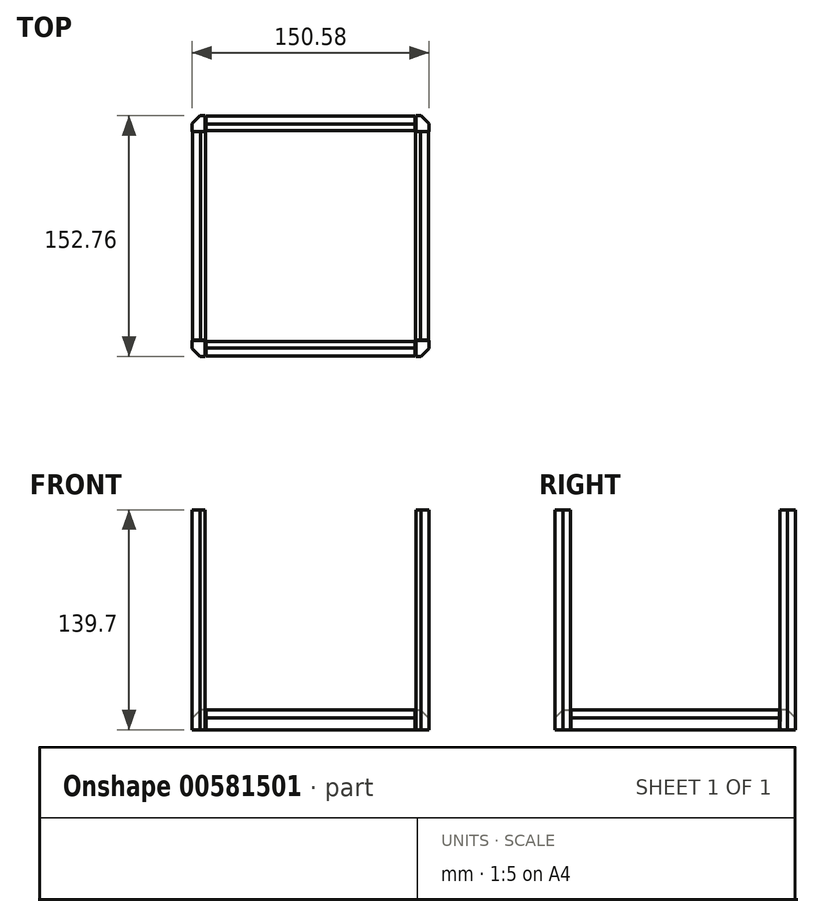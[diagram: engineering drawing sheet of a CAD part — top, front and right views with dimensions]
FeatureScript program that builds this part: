
annotation { "Feature Type Name" : "Feature", "Feature Type Description" : "" }
export const myFeature = defineFeature(function(context is Context, id is Id, definition is map)
    precondition{}
    {
        {
            var Q0;
            Q0=qCreatedBy(makeId("Top.planeOp"),FACE);
            var sketch = newSketch(context, id + "F0", { "sketchPlane" : qUnion([Q0])});
            skLineSegment(sketch, "E0.bottom", {"start": v(-75.29, 76.38) * mm, "end": v(-66.89, 76.38) * mm});
            skLineSegment(sketch, "E0.top", {"start": v(-75.29, 66.46) * mm, "end": v(-66.89, 66.46) * mm});
            skLineSegment(sketch, "E0.left", {"start": v(-75.29, 76.38) * mm, "end": v(-75.29, 66.46) * mm});
            skLineSegment(sketch, "E0.right", {"start": v(-66.89, 76.38) * mm, "end": v(-66.89, 66.46) * mm});
            skSolve(sketch);
        }
        {
            var Q0;
            Q0 = qSketchRegion(id + "F0", true);
            extrude(context, id + "F1", {"entities" : qUnion([Q0]), "depth" : 139.7 * mm, "offsetDistance" : 25.4 * mm});
        }
        {
            var Q0;
            Q0=makeQuery(id+"F1.opExtrude","SWEPT_BODY",BODY,{"disambiguationData":[OSD([sQuery(id+"F0.wireOp",EDGE,"E0.bottom"),sQuery(id+"F0.wireOp",EDGE,"E0.top"),sQuery(id+"F0.wireOp",EDGE,"E0.left"),sQuery(id+"F0.wireOp",EDGE,"E0.right")])]});
            var Q1;
            Q1=qCreatedBy(makeId("Right.planeOp"),FACE);
            mirror(context, id + "F2", {"entities" : qUnion([Q0]), "mirrorPlane" : qUnion([Q1])});
        }
        {
            var Q0;
            Q0=makeQuery(id+"F2.opPattern","COPY",BODY,{"derivedFrom":makeQuery(id+"F1.opExtrude","SWEPT_BODY",BODY,{"disambiguationData":[OSD([sQuery(id+"F0.wireOp",EDGE,"E0.bottom"),sQuery(id+"F0.wireOp",EDGE,"E0.top"),sQuery(id+"F0.wireOp",EDGE,"E0.left"),sQuery(id+"F0.wireOp",EDGE,"E0.right")])]}),"instanceName":"1"});
            var Q1;
            Q1=qCreatedBy(makeId("Front.planeOp"),FACE);
            mirror(context, id + "F3", {"entities" : qUnion([Q0]), "mirrorPlane" : qUnion([Q1])});
        }
        {
            var Q0;
            Q0=makeQuery(id+"F3.opPattern","COPY",BODY,{"derivedFrom":makeQuery(id+"F2.opPattern","COPY",BODY,{"derivedFrom":makeQuery(id+"F1.opExtrude","SWEPT_BODY",BODY,{"disambiguationData":[OSD([sQuery(id+"F0.wireOp",EDGE,"E0.bottom"),sQuery(id+"F0.wireOp",EDGE,"E0.top"),sQuery(id+"F0.wireOp",EDGE,"E0.left"),sQuery(id+"F0.wireOp",EDGE,"E0.right")])]}),"instanceName":"1"}),"instanceName":"1"});
            var Q1;
            Q1=qCreatedBy(makeId("Right.planeOp"),FACE);
            mirror(context, id + "F4", {"entities" : qUnion([Q0]), "mirrorPlane" : qUnion([Q1])});
        }
        {
            var Q0;
            Q0=qCreatedBy(makeId("Top.planeOp"),FACE);
            var sketch = newSketch(context, id + "F5", { "sketchPlane" : qUnion([Q0])});
            skLineSegment(sketch, "E1.bottom", {"start": v(-66.65, 66.31) * mm, "end": v(-75.03, 66.31) * mm});
            skLineSegment(sketch, "E1.top", {"start": v(-66.65, -66.13) * mm, "end": v(-75.03, -66.13) * mm});
            skLineSegment(sketch, "E1.left", {"start": v(-66.65, 66.31) * mm, "end": v(-66.65, -66.13) * mm});
            skLineSegment(sketch, "E1.right", {"start": v(-75.03, 66.31) * mm, "end": v(-75.03, -66.13) * mm});
            skSolve(sketch);
        }
        {
            var Q0;
            Q0 = qSketchRegion(id + "F5", true);
            extrude(context, id + "F6", {"entities" : qUnion([Q0]), "depth" : 12.7 * mm, "offsetDistance" : 25.4 * mm});
        }
        {
            var Q0;
            Q0=makeQuery(id+"F6.opExtrude","SWEPT_BODY",BODY,{"disambiguationData":[OSD([sQuery(id+"F5.wireOp",EDGE,"E1.bottom"),sQuery(id+"F5.wireOp",EDGE,"E1.top"),sQuery(id+"F5.wireOp",EDGE,"E1.left"),sQuery(id+"F5.wireOp",EDGE,"E1.right")])]});
            var Q1;
            Q1=makeQuery(id+"F1.opExtrude","SWEPT_BODY",BODY,{"disambiguationData":[OSD([sQuery(id+"F0.wireOp",EDGE,"E0.bottom"),sQuery(id+"F0.wireOp",EDGE,"E0.top"),sQuery(id+"F0.wireOp",EDGE,"E0.left"),sQuery(id+"F0.wireOp",EDGE,"E0.right")])]});
            var Q2;
            Q2=qCreatedBy(makeId("Right.planeOp"),FACE);
            mirror(context, id + "F7", {"operationType" : NewBodyOperationType.ADD, "entities" : qUnion([Q0, Q1]), "mirrorPlane" : qUnion([Q2])});
        }
        {
            var Q0;
            Q0=qCreatedBy(makeId("Top.planeOp"),FACE);
            var sketch = newSketch(context, id + "F8", { "sketchPlane" : qUnion([Q0])});
            skLineSegment(sketch, "E2.bottom", {"start": v(-66.46, -76.25) * mm, "end": v(66.33, -76.25) * mm});
            skLineSegment(sketch, "E2.top", {"start": v(-66.46, -67.1) * mm, "end": v(66.33, -67.1) * mm});
            skLineSegment(sketch, "E2.left", {"start": v(-66.46, -76.25) * mm, "end": v(-66.46, -67.1) * mm});
            skLineSegment(sketch, "E2.right", {"start": v(66.33, -76.25) * mm, "end": v(66.33, -67.1) * mm});
            skSolve(sketch);
        }
        {
            var Q0;
            Q0 = qSketchRegion(id + "F8", true);
            extrude(context, id + "F9", {"entities" : qUnion([Q0]), "depth" : 12.7 * mm, "offsetDistance" : 25.4 * mm});
        }
        {
            var Q0;
            Q0=makeQuery(id+"F9.opExtrude","SWEPT_BODY",BODY,{"disambiguationData":[OSD([sQuery(id+"F8.wireOp",EDGE,"E2.bottom"),sQuery(id+"F8.wireOp",EDGE,"E2.top"),sQuery(id+"F8.wireOp",EDGE,"E2.left"),sQuery(id+"F8.wireOp",EDGE,"E2.right")])]});
            var Q1;
            Q1=qCreatedBy(makeId("Front.planeOp"),FACE);
            mirror(context, id + "F10", {"entities" : qUnion([Q0]), "mirrorPlane" : qUnion([Q1])});
        }
        {
            var Q0;
            Q0=makeQuery(id+"F3.opPattern","COPY",EDGE,{"derivedFrom":makeQuery(id+"F2.opPattern","COPY",EDGE,{"derivedFrom":makeQuery(id+"F1.opExtrude","SWEPT_EDGE",EDGE,{"disambiguationData":[OSD([sQuery(id+"F0.wireOp",EDGE,"E0.bottom"),sQuery(id+"F0.wireOp",EDGE,"E0.left")])]}),"instanceName":"1"}),"instanceName":"1"});
            var Q1;
            Q1=makeQuery(id+"F2.opPattern","COPY",EDGE,{"derivedFrom":makeQuery(id+"F1.opExtrude","SWEPT_EDGE",EDGE,{"disambiguationData":[OSD([sQuery(id+"F0.wireOp",EDGE,"E0.bottom"),sQuery(id+"F0.wireOp",EDGE,"E0.left")])]}),"instanceName":"1"});
            var Q2;
            Q2=makeQuery(id+"F4.opPattern","COPY",EDGE,{"derivedFrom":makeQuery(id+"F3.opPattern","COPY",EDGE,{"derivedFrom":makeQuery(id+"F2.opPattern","COPY",EDGE,{"derivedFrom":makeQuery(id+"F1.opExtrude","SWEPT_EDGE",EDGE,{"disambiguationData":[OSD([sQuery(id+"F0.wireOp",EDGE,"E0.bottom"),sQuery(id+"F0.wireOp",EDGE,"E0.left")])]}),"instanceName":"1"}),"instanceName":"1"}),"instanceName":"1"});
            var Q3;
            Q3=makeQuery(id+"F1.opExtrude","SWEPT_EDGE",EDGE,{"disambiguationData":[OSD([sQuery(id+"F0.wireOp",EDGE,"E0.bottom"),sQuery(id+"F0.wireOp",EDGE,"E0.left")])]});
            chamfer(context, id + "F11", {"entities" : qUnion([Q0, Q1, Q2, Q3]), "width" : 5.08 * mm, "tangentPropagation" : true});
        }
        {
            var Q0;
            Q0=makeQuery(id+"F9.opExtrude","CAP_EDGE",EDGE,{"disambiguationData":[OSD([sQuery(id+"F8.wireOp",EDGE,"E2.bottom")])],"isStart":false});
            var Q1;
            Q1=makeQuery(id+"F7.opPattern","COPY",EDGE,{"derivedFrom":makeQuery(id+"F6.opExtrude","CAP_EDGE",EDGE,{"disambiguationData":[OSD([sQuery(id+"F5.wireOp",EDGE,"E1.right")])],"isStart":false}),"instanceName":"1"});
            var Q2;
            Q2=makeQuery(id+"F10.opPattern","COPY",EDGE,{"derivedFrom":makeQuery(id+"F9.opExtrude","CAP_EDGE",EDGE,{"disambiguationData":[OSD([sQuery(id+"F8.wireOp",EDGE,"E2.bottom")])],"isStart":false}),"instanceName":"1"});
            var Q3;
            Q3=makeQuery(id+"F6.opExtrude","CAP_EDGE",EDGE,{"disambiguationData":[OSD([sQuery(id+"F5.wireOp",EDGE,"E1.right")])],"isStart":false});
            chamfer(context, id + "F12", {"entities" : qUnion([Q0, Q1, Q2, Q3]), "width" : 5.08 * mm, "tangentPropagation" : true});
        }
    });
